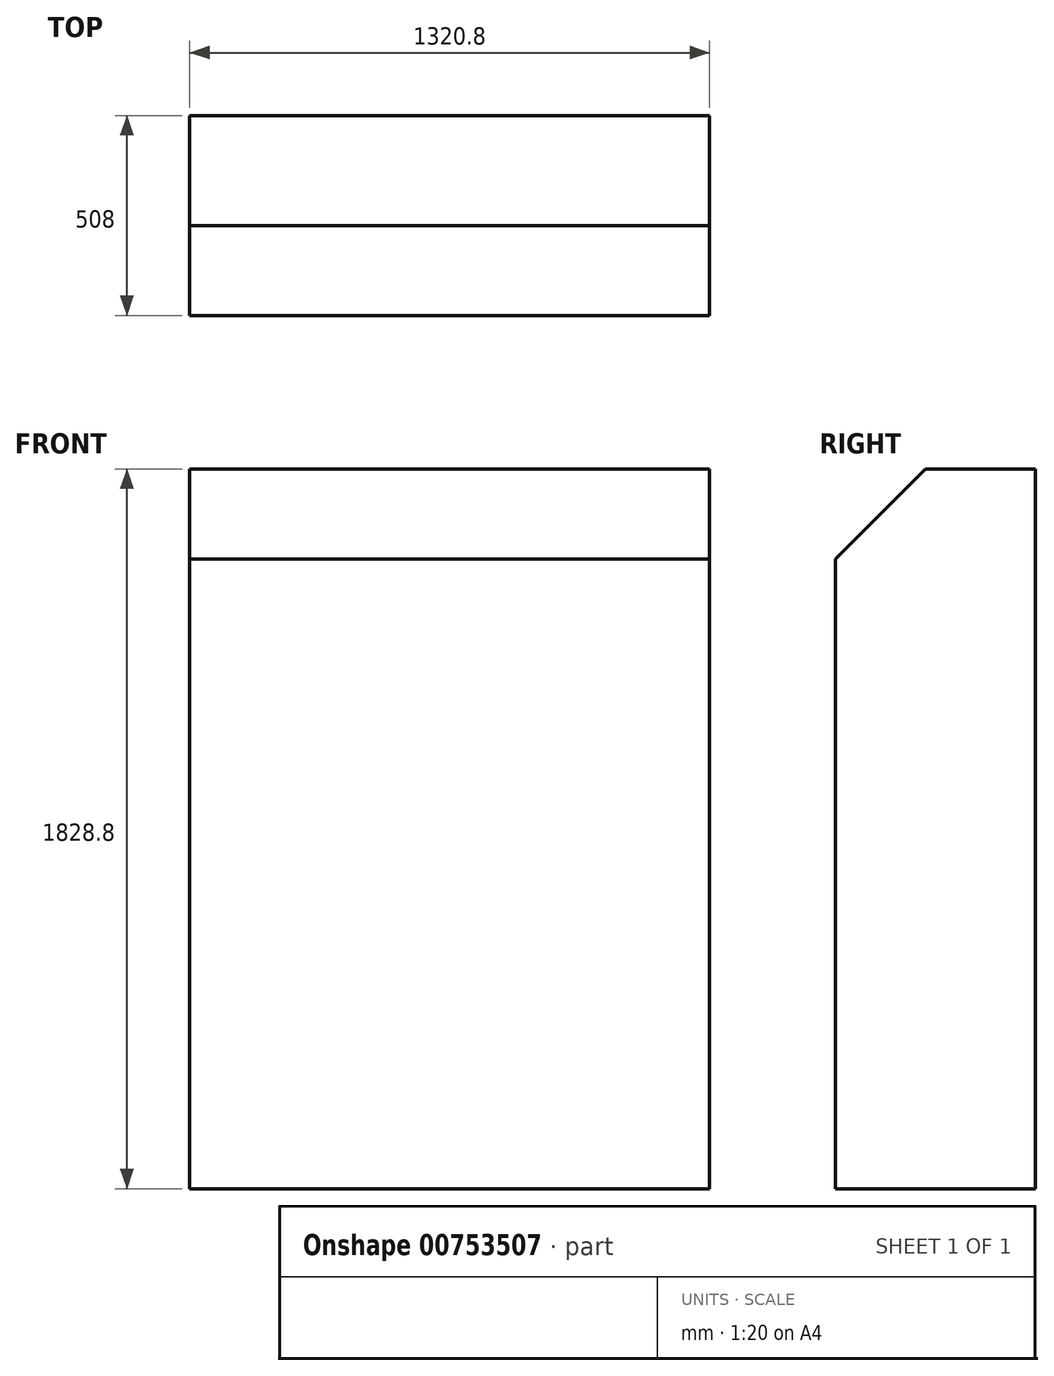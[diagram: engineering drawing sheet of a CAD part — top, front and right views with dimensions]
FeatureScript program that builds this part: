
annotation { "Feature Type Name" : "Feature", "Feature Type Description" : "" }
export const myFeature = defineFeature(function(context is Context, id is Id, definition is map)
    precondition{}
    {
        {
            var Q0;
            Q0=qCreatedBy(makeId("Right.planeOp"),FACE);
            var sketch = newSketch(context, id + "F0", { "sketchPlane" : qUnion([Q0])});
            skLineSegment(sketch, "E0", {"start": v(-254, -914.4) * mm, "end": v(254, -914.4) * mm});
            skLineSegment(sketch, "E1", {"start": v(254, -914.4) * mm, "end": v(254, 914.4) * mm});
            skLineSegment(sketch, "E2", {"start": v(254, 914.4) * mm, "end": v(-25.4, 914.4) * mm});
            skLineSegment(sketch, "E3", {"start": v(-25.4, 914.4) * mm, "end": v(-254, 685.8) * mm});
            skLineSegment(sketch, "E4", {"start": v(-254, 685.8) * mm, "end": v(-254, -914.4) * mm});
            skSolve(sketch);
        }
        {
            var Q0;
            Q0=makeQuery(id+"F0.imprint","IMPRINT",FACE,{"disambiguationData":[TD([[makeQuery(id+"F0.imprint","IMPRINT",EDGE,{"derivedFrom":sQuery(id+"F0.wireOp",EDGE,"E0")}),1.0]])]});
            extrude(context, id + "F1", {"entities" : qUnion([Q0]), "endBound" : BoundingType.SYMMETRIC, "depth" : 1320.8 * mm, "offsetDistance" : 25.4 * mm});
        }
    });
